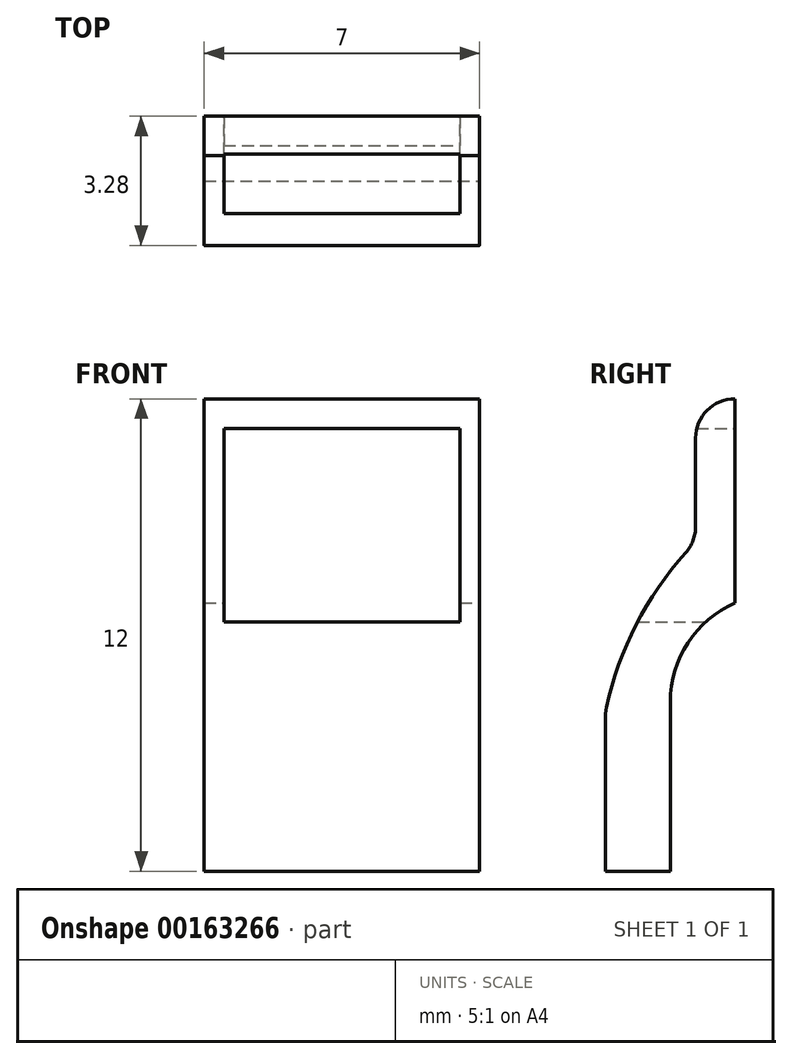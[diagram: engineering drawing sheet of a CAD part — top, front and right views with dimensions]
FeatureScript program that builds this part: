
annotation { "Feature Type Name" : "Feature", "Feature Type Description" : "" }
export const myFeature = defineFeature(function(context is Context, id is Id, definition is map)
    precondition{}
    {
        {
            var Q0;
            Q0=qCreatedBy(makeId("Right.planeOp"),FACE);
            var sketch = newSketch(context, id + "F0", { "sketchPlane" : qUnion([Q0])});
            skLineSegment(sketch, "E0", {"start": v(-0.07, 0.58) * mm, "end": v(-0.07, 12.58) * mm});
            skLineSegment(sketch, "E1", {"start": v(-0.07, 12.58) * mm, "end": v(-0.07, 12.58) * mm});
            skLineSegment(sketch, "E2", {"start": v(-1.07, 11.58) * mm, "end": v(-1.07, 9.34) * mm});
            skArc(sketch, "E3", {"start": v(-1.32, 8.67) * mm, "mid": v(-2.58, 6.84) * mm, "end": v(-3.33, 4.75) * mm});
            skLineSegment(sketch, "E4", {"start": v(-3.35, 4.53) * mm, "end": v(-3.35, 0.58) * mm});
            skLineSegment(sketch, "E5", {"start": v(-3.35, 0.58) * mm, "end": v(-0.07, 0.58) * mm});
            skPoint(sketch, "E6.visualSharp", {"position": v(-1.07, 8.94) * mm});
            skArc(sketch, "E6.filletArc", {"start": v(-1.32, 8.67) * mm, "mid": v(-1.13, 8.98) * mm, "end": v(-1.07, 9.34) * mm});
            skPoint(sketch, "E7.visualSharp", {"position": v(-1.07, 12.58) * mm});
            skArc(sketch, "E7.filletArc", {"start": v(-0.07, 12.58) * mm, "mid": v(-0.77, 12.29) * mm, "end": v(-1.07, 11.58) * mm});
            skPoint(sketch, "E8.visualSharp", {"position": v(-3.35, 4.64) * mm});
            skArc(sketch, "E8.filletArc", {"start": v(-3.33, 4.75) * mm, "mid": v(-3.35, 4.64) * mm, "end": v(-3.35, 4.53) * mm});
            skSolve(sketch);
        }
        {
            var Q0;
            Q0 = qSketchRegion(id + "F0", true);
            extrude(context, id + "F1", {"entities" : qUnion([Q0]), "depth" : 7 * mm});
        }
        {
            var Q0;
            Q0=makeQuery(id+"F1.opExtrude","SWEPT_FACE",FACE,{"disambiguationData":[OSD([sQuery(id+"F0.wireOp",EDGE,"E0")])]});
            var sketch = newSketch(context, id + "F2", { "sketchPlane" : qUnion([Q0])});
            skLineSegment(sketch, "E9.bottom", {"start": v(-6.5, 11.83) * mm, "end": v(-0.5, 11.83) * mm});
            skLineSegment(sketch, "E9.top", {"start": v(-6.5, 6.91) * mm, "end": v(-0.5, 6.91) * mm});
            skLineSegment(sketch, "E9.left", {"start": v(-6.5, 11.83) * mm, "end": v(-6.5, 6.91) * mm});
            skLineSegment(sketch, "E9.right", {"start": v(-0.5, 11.83) * mm, "end": v(-0.5, 6.91) * mm});
            skSolve(sketch);
        }
        {
            var Q0;
            Q0 = qSketchRegion(id + "F2", true);
            extrude(context, id + "F3", {"entities" : qUnion([Q0]), "operationType" : NewBodyOperationType.REMOVE, "endBound" : BoundingType.THROUGH_ALL, "oppositeDirection" : true, "depth" : 25 * mm});
        }
        {
            var Q0;
            Q0=makeQuery(id+"F1.opExtrude","CAP_FACE",FACE,{"disambiguationData":[OSD([sQuery(id+"F0.wireOp",EDGE,"E0"),sQuery(id+"F0.wireOp",EDGE,"E2"),sQuery(id+"F0.wireOp",EDGE,"E3"),sQuery(id+"F0.wireOp",EDGE,"E4"),sQuery(id+"F0.wireOp",EDGE,"E5"),sQuery(id+"F0.wireOp",EDGE,"E6.filletArc"),sQuery(id+"F0.wireOp",EDGE,"E7.filletArc"),sQuery(id+"F0.wireOp",EDGE,"E8.filletArc")])],"isStart":false});
            var sketch = newSketch(context, id + "F4", { "sketchPlane" : qUnion([Q0])});
            skLineSegment(sketch, "E10.bottom", {"start": v(-1.7, 0.58) * mm, "end": v(-0.07, 0.58) * mm});
            skLineSegment(sketch, "E10.left", {"start": v(-1.7, 0.58) * mm, "end": v(-1.7, 4.89) * mm});
            skLineSegment(sketch, "E10.right", {"start": v(-0.07, 0.58) * mm, "end": v(-0.07, 2.01) * mm});
            skArc(sketch, "E11", {"start": v(-0.07, 7.4) * mm, "mid": v(-1.26, 6.39) * mm, "end": v(-1.7, 4.89) * mm});
            skLineSegment(sketch, "E12", {"start": v(-0.07, 7.4) * mm, "end": v(-0.07, 2.01) * mm});
            skSolve(sketch);
        }
        {
            var Q0;
            Q0 = qSketchRegion(id + "F4", true);
            extrude(context, id + "F5", {"entities" : qUnion([Q0]), "operationType" : NewBodyOperationType.REMOVE, "endBound" : BoundingType.THROUGH_ALL, "oppositeDirection" : true, "depth" : 25 * mm});
        }
    });
